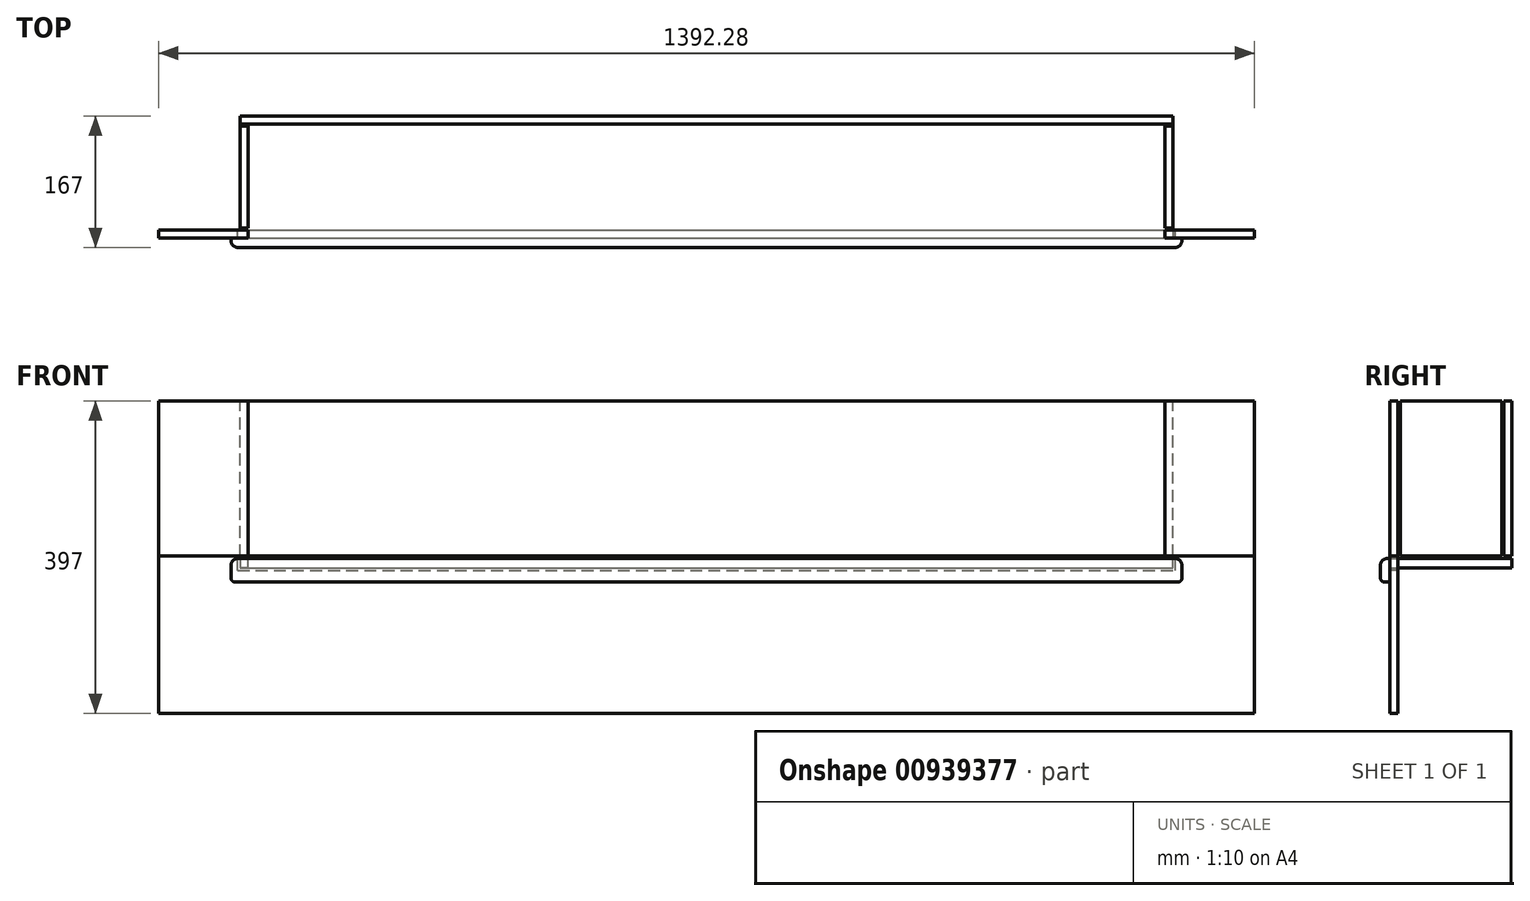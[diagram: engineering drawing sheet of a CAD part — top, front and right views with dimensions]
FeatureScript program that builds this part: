
annotation { "Feature Type Name" : "Feature", "Feature Type Description" : "" }
export const myFeature = defineFeature(function(context is Context, id is Id, definition is map)
    precondition{}
    {
        {
            assignVariable(context, id + "F0", {"name" : "thk", "anyValue" : 12});
        }
        {
            assignVariable(context, id + "F1", {"name" : "csht", "anyValue" : 6});
        }
        {
            assignVariable(context, id + "F2", {"name" : "fila", "anyValue" : 9});
        }
        {
            assignVariable(context, id + "F3", {"name" : "filb", "anyValue" : 5});
        }
        {
            assignVariable(context, id + "F4", {"name" : "t", "anyValue" : 16});
        }
        {
            assignVariable(context, id + "F5", {"variableType" : VariableType.LENGTH, "name" : "g", "lengthValue" : 3 * mm});
        }
        {
            var Q0;
            Q0=qCreatedBy(makeId("Top.planeOp"),FACE);
            var sketch = newSketch(context, id + "F6", { "sketchPlane" : qUnion([Q0])});
            skLineSegment(sketch, "E0.bottom", {"start": v(-592.5, 0) * mm, "end": v(592.5, 0) * mm});
            skLineSegment(sketch, "E0.top", {"start": v(-592.5, -155) * mm, "end": v(592.5, -155) * mm});
            skLineSegment(sketch, "E0.left", {"start": v(-592.5, 0) * mm, "end": v(-592.5, -155) * mm});
            skLineSegment(sketch, "E0.right", {"start": v(592.5, 0) * mm, "end": v(592.5, -155) * mm});
            skLineSegment(sketch, "E1.bottom", {"start": v(-604, -155) * mm, "end": v(604, -155) * mm});
            skLineSegment(sketch, "E1.top", {"start": v(-604, -167) * mm, "end": v(604, -167) * mm});
            skLineSegment(sketch, "E1.left", {"start": v(-604, -155) * mm, "end": v(-604, -167) * mm});
            skLineSegment(sketch, "E1.right", {"start": v(604, -155) * mm, "end": v(604, -167) * mm});
            skLineSegment(sketch, "E2", {"start": v(-201.33, -233.8) * mm, "end": v(-201.33, -67.33) * mm, "construction": true});
            skLineSegment(sketch, "E3", {"start": v(201.33, -233.8) * mm, "end": v(201.33, -67.33) * mm, "construction": true});
            skLineSegment(sketch, "E4", {"start": v(0, -92.62) * mm, "end": v(0, -203.26) * mm, "construction": true});
            skPoint(sketch, "E4.startSnap0", {"position": v(0, -155) * mm});
            skPoint(sketch, "E4.endSnap0", {"position": v(0, -167) * mm});
            skSolve(sketch);
        }
        {
            var Q0;
            Q0=makeQuery(id+"F6.imprint","IMPRINT",FACE,{"disambiguationData":[TD([[makeQuery(id+"F6.imprint","IMPRINT",EDGE,{"derivedFrom":sQuery(id+"F6.wireOp",EDGE,"E0.bottom")}),-1.0]])]});
            var Q1;
            Q1=makeQuery(id+"F6.imprint","IMPRINT",FACE,{"disambiguationData":[TD([[makeQuery(id+"F6.imprint","IMPRINT",EDGE,{"derivedFrom":sQuery(id+"F6.wireOp",EDGE,"E1.top")}),1.0]])]});
            extrude(context, id + "F7", {"entities" : qUnion([Q0, Q1]), "oppositeDirection" : true, "depth" : (getVariable(context, 'thk')) * mm, "offsetDistance" : 25 * mm});
        }
        {
            var Q0;
            Q0=qCreatedBy(makeId("Top.planeOp"),FACE);
            var sketch = newSketch(context, id + "F8", { "sketchPlane" : qUnion([Q0])});
            skLineSegment(sketch, "E5.bottom", {"start": v(-604, -167) * mm, "end": v(604, -167) * mm});
            skLineSegment(sketch, "E5.top", {"start": v(-604, -155) * mm, "end": v(604, -155) * mm});
            skLineSegment(sketch, "E5.left", {"start": v(-604, -167) * mm, "end": v(-604, -155) * mm});
            skLineSegment(sketch, "E5.right", {"start": v(604, -167) * mm, "end": v(604, -155) * mm});
            skSolve(sketch);
        }
        {
            var Q0;
            Q0 = qSketchRegion(id + "F8", true);
            extrude(context, id + "F9", {"entities" : qUnion([Q0]), "oppositeDirection" : true, "depth" : 30 * mm, "offsetDistance" : 25 * mm});
        }
        {
            var Q0;
            Q0=makeQuery(id+"F9.opExtrude","SWEPT_BODY",BODY,{"disambiguationData":[OSD([sQuery(id+"F8.wireOp",EDGE,"E5.bottom"),sQuery(id+"F8.wireOp",EDGE,"E5.top"),sQuery(id+"F8.wireOp",EDGE,"E5.left"),sQuery(id+"F8.wireOp",EDGE,"E5.right")])]});
            var Q1;
            Q1=makeQuery(id+"FpJi88sFKc314K6_2.opPattern","COPY",BODY,{"derivedFrom":makeQuery(id+"F9.opExtrude","SWEPT_BODY",BODY,{"disambiguationData":[OSD([sQuery(id+"F8.wireOp",EDGE,"E5.bottom"),sQuery(id+"F8.wireOp",EDGE,"E5.top"),sQuery(id+"F8.wireOp",EDGE,"E5.left"),sQuery(id+"F8.wireOp",EDGE,"E5.right")])]}),"instanceName":"1"});
            var Q2;
            Q2=makeQuery(id+"F7.opExtrude","SWEPT_BODY",BODY,{"disambiguationData":[OSD([sQuery(id+"F6.wireOp",EDGE,"E0.bottom"),sQuery(id+"F6.wireOp",EDGE,"E0.left"),sQuery(id+"F6.wireOp",EDGE,"E0.right"),sQuery(id+"F6.wireOp",EDGE,"E1.bottom"),sQuery(id+"F6.wireOp",EDGE,"E1.top"),sQuery(id+"F6.wireOp",EDGE,"E1.left"),sQuery(id+"F6.wireOp",EDGE,"E1.right")])]});
            booleanBodies(context, id + "F10", {"operationType" : BooleanOperationType.SUBTRACTION, "tools" : qUnion([Q0, Q1]), "targets" : qUnion([Q2]), "keepTools" : true});
        }
        {
            var Q0;
            Q0=makeQuery(id+"F9.opExtrude","CAP_EDGE",EDGE,{"disambiguationData":[OSD([sQuery(id+"F8.wireOp",EDGE,"E5.right")])],"isStart":true});
            var Q1;
            Q1=makeQuery(id+"F9.opExtrude","CAP_EDGE",EDGE,{"disambiguationData":[OSD([sQuery(id+"F8.wireOp",EDGE,"E5.bottom")])],"isStart":true});
            var Q2;
            Q2=makeQuery(id+"F9.opExtrude","CAP_EDGE",EDGE,{"disambiguationData":[OSD([sQuery(id+"F8.wireOp",EDGE,"E5.left")])],"isStart":true});
            fillet(context, id + "F11", {"entities" : qUnion([Q0, Q1, Q2]), "radius" : (getVariable(context, 'fila')) * mm, "tangentPropagation" : true, "allowEdgeOverflow" : false});
        }
        {
            var Q0;
            Q0=makeQuery(id+"F9.opExtrude","SWEPT_EDGE",EDGE,{"disambiguationData":[OSD([sQuery(id+"F8.wireOp",EDGE,"E5.bottom"),sQuery(id+"F8.wireOp",EDGE,"E5.left")])]});
            var Q1;
            Q1=makeQuery(id+"F9.opExtrude","SWEPT_EDGE",EDGE,{"disambiguationData":[OSD([sQuery(id+"F8.wireOp",EDGE,"E5.bottom"),sQuery(id+"F8.wireOp",EDGE,"E5.right")])]});
            fillet(context, id + "F12", {"entities" : qUnion([Q0, Q1]), "radius" : (getVariable(context, 'fila')) * mm, "tangentPropagation" : true, "allowEdgeOverflow" : false});
        }
        {
            var Q0;
            Q0=makeQuery(id+"F7.opExtrude","SWEPT_BODY",BODY,{"disambiguationData":[OSD([sQuery(id+"F6.wireOp",EDGE,"E0.bottom"),sQuery(id+"F6.wireOp",EDGE,"E0.left"),sQuery(id+"F6.wireOp",EDGE,"E0.right"),sQuery(id+"F6.wireOp",EDGE,"E1.bottom"),sQuery(id+"F6.wireOp",EDGE,"E1.top"),sQuery(id+"F6.wireOp",EDGE,"E1.left"),sQuery(id+"F6.wireOp",EDGE,"E1.right")])]});
            var Q1;
            Q1=makeQuery(id+"F9.opExtrude","SWEPT_BODY",BODY,{"disambiguationData":[OSD([sQuery(id+"F8.wireOp",EDGE,"E5.bottom"),sQuery(id+"F8.wireOp",EDGE,"E5.top"),sQuery(id+"F8.wireOp",EDGE,"E5.left"),sQuery(id+"F8.wireOp",EDGE,"E5.right")])]});
            booleanBodies(context, id + "F13", {"operationType" : BooleanOperationType.UNION, "tools" : qUnion([Q0, Q1])});
        }
        {
            var Q0;
            Q0=makeQuery(id+"F9.opExtrude","CAP_EDGE",EDGE,{"disambiguationData":[OSD([sQuery(id+"F8.wireOp",EDGE,"E5.right")])],"isStart":false});
            fillet(context, id + "F14", {"entities" : qUnion([Q0]), "radius" : (getVariable(context, 'filb')) * mm, "tangentPropagation" : true, "allowEdgeOverflow" : false});
        }
        {
            var Q0;
            Q0=qCreatedBy(makeId("Top.planeOp"),FACE);
            cPlane(context, id + "F15", {"entities" : qUnion([Q0]), "cplaneType" : CPlaneType.OFFSET, "offset" : 200 * mm, "width" : 150 * mm, "height" : 150 * mm});
        }
        {
            var Q0;
            Q0=qCreatedBy(id+"F15.planeOp",FACE);
            var sketch = newSketch(context, id + "F16", { "sketchPlane" : qUnion([Q0])});
            skLineSegment(sketch, "E6", {"start": v(-592.5, 0) * mm, "end": v(592.5, 0) * mm});
            skLineSegment(sketch, "E7", {"start": v(592.5, 0) * mm, "end": v(592.5, -142) * mm});
            skLineSegment(sketch, "E8", {"start": v(592.5, -142) * mm, "end": v(582.5, -142) * mm});
            skLineSegment(sketch, "E9", {"start": v(582.5, -142) * mm, "end": v(582.5, -10) * mm});
            skLineSegment(sketch, "E10", {"start": v(582.5, -10) * mm, "end": v(-582.5, -10) * mm});
            skLineSegment(sketch, "E11", {"start": v(-582.5, -10) * mm, "end": v(-582.5, -142) * mm});
            skLineSegment(sketch, "E12", {"start": v(-582.5, -142) * mm, "end": v(-592.5, -142) * mm});
            skLineSegment(sketch, "E13", {"start": v(-592.5, -142) * mm, "end": v(-592.5, 0) * mm});
            skLineSegment(sketch, "E14", {"start": v(582.5, -145) * mm, "end": v(582.5, -155) * mm});
            skLineSegment(sketch, "E15", {"start": v(582.5, -155) * mm, "end": v(696.14, -155) * mm});
            skLineSegment(sketch, "E16", {"start": v(582.5, -145) * mm, "end": v(696.14, -145) * mm});
            skLineSegment(sketch, "E17", {"start": v(696.14, -145) * mm, "end": v(696.14, -155) * mm});
            skLineSegment(sketch, "E18.MirrorCS", {"start": v(-582.5, -145) * mm, "end": v(-696.14, -145) * mm});
            skLineSegment(sketch, "E19.MirrorCS", {"start": v(-696.14, -145) * mm, "end": v(-696.14, -155) * mm});
            skLineSegment(sketch, "E20.MirrorCS", {"start": v(-582.5, -155) * mm, "end": v(-696.14, -155) * mm});
            skLineSegment(sketch, "E21.MirrorCS", {"start": v(-582.5, -145) * mm, "end": v(-582.5, -155) * mm});
            skLineSegment(sketch, "E22", {"start": v(-582.5, -10) * mm, "end": v(-592.5, -10) * mm});
            skLineSegment(sketch, "E23", {"start": v(-582.5, -13) * mm, "end": v(-592.5, -13) * mm});
            skLineSegment(sketch, "E24", {"start": v(582.5, -13) * mm, "end": v(592.5, -13) * mm});
            skLineSegment(sketch, "E25", {"start": v(582.5, -10) * mm, "end": v(592.5, -10) * mm});
            skSolve(sketch);
        }
        {
            var Q0;
            Q0=makeQuery(id+"F16.imprint","IMPRINT",FACE,{"disambiguationData":[TD([[makeQuery(id+"F16.imprint","IMPRINT",EDGE,{"derivedFrom":sQuery(id+"F16.wireOp",EDGE,"E6")}),-1.0]])]});
            var Q1;
            Q1=makeQuery(id+"F16.imprint","IMPRINT",FACE,{"disambiguationData":[TD([[makeQuery(id+"F16.imprint","IMPRINT",EDGE,{"derivedFrom":sQuery(id+"F16.wireOp",EDGE,"E18.MirrorCS")}),1.0]])]});
            var Q2;
            Q2=makeQuery(id+"F16.imprint","IMPRINT",FACE,{"disambiguationData":[TD([[makeQuery(id+"F16.imprint","IMPRINT",EDGE,{"derivedFrom":sQuery(id+"F16.wireOp",EDGE,"E14")}),1.0]])]});
            var Q3;
            {var subQ0=sQuery(id+"F16.wireOp",EDGE,"E12");Q3=makeQuery(id+"F16.imprint","IMPRINT",FACE,{"disambiguationData":[TD([[makeQuery(id+"F16.imprint","IMPRINT",EDGE,{"derivedFrom":subQ0}),-1.0]])]});}
            var Q4;
            {var subQ0=sQuery(id+"F16.wireOp",EDGE,"E8");Q4=makeQuery(id+"F16.imprint","IMPRINT",FACE,{"disambiguationData":[TD([[makeQuery(id+"F16.imprint","IMPRINT",EDGE,{"derivedFrom":subQ0}),-1.0]])]});}
            var Q5;
            Q5=makeQuery(id+"F13.opBoolean","MERGE",FACE,{"derivedFrom":[makeQuery(id+"F7.opExtrude","CAP_FACE",FACE,{"disambiguationData":[OSD([sQuery(id+"F6.wireOp",EDGE,"E0.bottom"),sQuery(id+"F6.wireOp",EDGE,"E0.left"),sQuery(id+"F6.wireOp",EDGE,"E0.right"),sQuery(id+"F6.wireOp",EDGE,"E1.bottom"),sQuery(id+"F6.wireOp",EDGE,"E1.top"),sQuery(id+"F6.wireOp",EDGE,"E1.left"),sQuery(id+"F6.wireOp",EDGE,"E1.right")])],"isStart":true}),makeQuery(id+"F9.opExtrude","CAP_FACE",FACE,{"disambiguationData":[OSD([sQuery(id+"F8.wireOp",EDGE,"E5.bottom"),sQuery(id+"F8.wireOp",EDGE,"E5.top"),sQuery(id+"F8.wireOp",EDGE,"E5.left"),sQuery(id+"F8.wireOp",EDGE,"E5.right")])],"isStart":true})]});
            extrude(context, id + "F17", {"entities" : qUnion([Q0, Q1, Q2, Q3, Q4]), "endBound" : BoundingType.UP_TO_SURFACE, "oppositeDirection" : true, "depth" : 25 * mm, "endBoundEntityFace" : qUnion([Q5]), "hasOffset" : true, "offsetDistance" : getVariable(context, 'g')});
        }
        {
            var Q0;
            Q0=makeQuery(id+"F17.opExtrude","CAP_FACE",FACE,{"disambiguationData":[OSD([sQuery(id+"F16.wireOp",EDGE,"E18.MirrorCS"),sQuery(id+"F16.wireOp",EDGE,"E19.MirrorCS"),sQuery(id+"F16.wireOp",EDGE,"E20.MirrorCS"),sQuery(id+"F16.wireOp",EDGE,"E21.MirrorCS")])],"isStart":false});
            extrude(context, id + "F18", {"entities" : qUnion([Q0]), "depth" : 200 * mm, "offsetDistance" : 25 * mm});
        }
        {
            var Q0;
            Q0=makeQuery(id+"F18.opExtrude","SWEPT_FACE",FACE,{"disambiguationData":[OSD([sQuery(id+"F16.wireOp",EDGE,"E21.MirrorCS")])]});
            extrude(context, id + "F19", {"entities" : qUnion([Q0]), "operationType" : NewBodyOperationType.REMOVE, "oppositeDirection" : true, "depth" : (getVariable(context, 't') - getVariable(context, 'csht')) * mm + getVariable(context, 'g'), "offsetDistance" : 25 * mm});
        }
        {
            var Q0;
            Q0=makeQuery(id+"F18.opExtrude","SWEPT_BODY",BODY,{"disambiguationData":[OSD([sQuery(id+"F16.wireOp",EDGE,"E18.MirrorCS"),sQuery(id+"F16.wireOp",EDGE,"E19.MirrorCS"),sQuery(id+"F16.wireOp",EDGE,"E20.MirrorCS"),sQuery(id+"F16.wireOp",EDGE,"E21.MirrorCS")])]});
            var Q1;
            Q1=qCreatedBy(makeId("Right.planeOp"),FACE);
            mirror(context, id + "F20", {"entities" : qUnion([Q0]), "mirrorPlane" : qUnion([Q1])});
        }
        {
            var Q0;
            Q0=makeQuery(id+"F20.opPattern","COPY",FACE,{"derivedFrom":makeQuery(id+"F18.opExtrude","CAP_FACE",FACE,{"disambiguationData":[OSD([sQuery(id+"F16.wireOp",EDGE,"E18.MirrorCS"),sQuery(id+"F16.wireOp",EDGE,"E19.MirrorCS"),sQuery(id+"F16.wireOp",EDGE,"E20.MirrorCS"),sQuery(id+"F16.wireOp",EDGE,"E21.MirrorCS")])],"isStart":false}),"instanceName":"1"});
            var sketch = newSketch(context, id + "F21", { "sketchPlane" : qUnion([Q0])});
            skLineSegment(sketch, "E26.bottom", {"start": v(-595.5, 145) * mm, "end": v(595.5, 145) * mm});
            skLineSegment(sketch, "E26.top", {"start": v(-595.5, 155) * mm, "end": v(595.5, 155) * mm});
            skLineSegment(sketch, "E26.left", {"start": v(-595.5, 145) * mm, "end": v(-595.5, 155) * mm});
            skLineSegment(sketch, "E26.right", {"start": v(595.5, 145) * mm, "end": v(595.5, 155) * mm});
            skSolve(sketch);
        }
        {
            var Q0;
            Q0=makeQuery(id+"F21.imprint","IMPRINT",FACE,{"disambiguationData":[TD([[makeQuery(id+"F21.imprint","IMPRINT",EDGE,{"derivedFrom":sQuery(id+"F21.wireOp",EDGE,"E26.bottom")}),1.0]])]});
            var Q1;
            Q1=makeQuery(id+"F7.opExtrude","CAP_FACE",FACE,{"disambiguationData":[OSD([sQuery(id+"F6.wireOp",EDGE,"E0.bottom"),sQuery(id+"F6.wireOp",EDGE,"E0.left"),sQuery(id+"F6.wireOp",EDGE,"E0.right"),sQuery(id+"F6.wireOp",EDGE,"E1.bottom"),sQuery(id+"F6.wireOp",EDGE,"E1.top"),sQuery(id+"F6.wireOp",EDGE,"E1.left"),sQuery(id+"F6.wireOp",EDGE,"E1.right")])],"isStart":false});
            extrude(context, id + "F22", {"entities" : qUnion([Q0]), "operationType" : NewBodyOperationType.ADD, "endBound" : BoundingType.UP_TO_SURFACE, "oppositeDirection" : true, "depth" : 25 * mm, "endBoundEntityFace" : qUnion([Q1]), "hasOffset" : true, "offsetDistance" : getVariable(context, 'g')});
        }
    });
